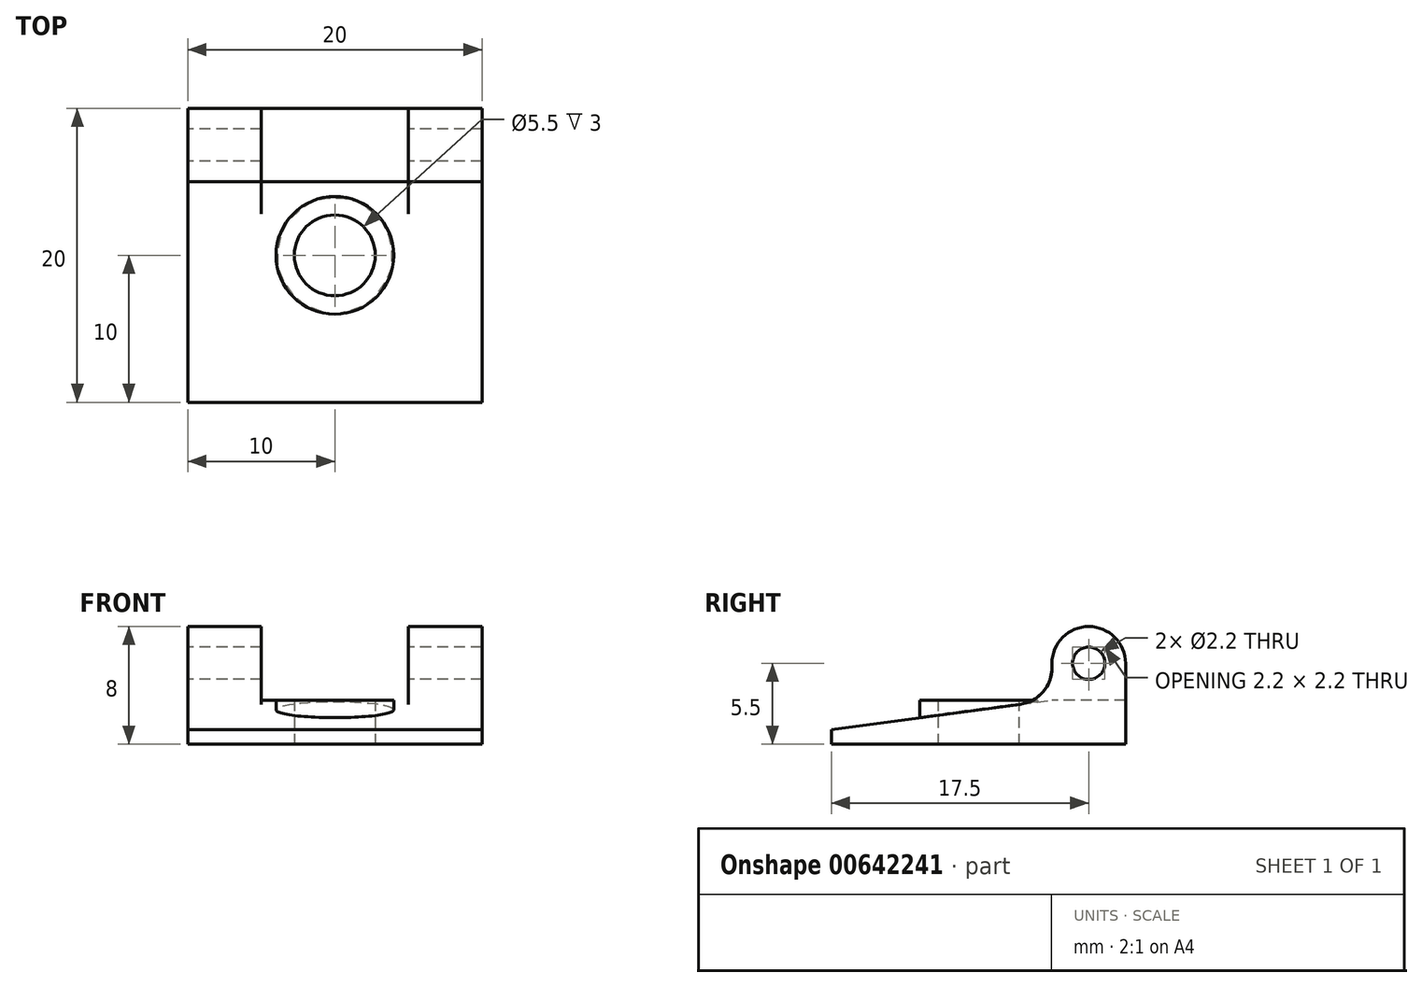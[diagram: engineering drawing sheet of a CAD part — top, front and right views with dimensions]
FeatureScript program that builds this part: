
annotation { "Feature Type Name" : "Feature", "Feature Type Description" : "" }
export const myFeature = defineFeature(function(context is Context, id is Id, definition is map)
    precondition{}
    {
        {
            var Q0;
            Q0=qCreatedBy(makeId("Top.planeOp"),FACE);
            var sketch = newSketch(context, id + "F0", { "sketchPlane" : qUnion([Q0])});
            skLineSegment(sketch, "E0.bottom", {"start": v(0, 0) * mm, "end": v(20, 0) * mm});
            skLineSegment(sketch, "E0.top", {"start": v(0, 20) * mm, "end": v(20, 20) * mm});
            skLineSegment(sketch, "E0.left", {"start": v(0, 0) * mm, "end": v(0, 20) * mm});
            skLineSegment(sketch, "E0.right", {"start": v(20, 0) * mm, "end": v(20, 20) * mm});
            skCircle(sketch, "E1", {"center": v(10, 10) * mm, "radius": 2.75 * mm});
            skCircle(sketch, "E2", {"center": v(10, 10) * mm, "radius": 4 * mm});
            skSolve(sketch);
        }
        {
            var Q0;
            Q0=makeQuery(id+"F0.imprint","IMPRINT",FACE,{"disambiguationData":[TD([[makeQuery(id+"F0.imprint","IMPRINT",EDGE,{"derivedFrom":sQuery(id+"F0.wireOp",EDGE,"E0.bottom")}),1.0]])]});
            extrude(context, id + "F1", {"entities" : qUnion([Q0]), "depth" : 4 * mm, "offsetDistance" : 25 * mm});
        }
        {
            var Q0;
            Q0=makeQuery(id+"F1.opExtrude","CAP_FACE",FACE,{"disambiguationData":[OSD([sQuery(id+"F0.wireOp",EDGE,"E0.bottom"),sQuery(id+"F0.wireOp",EDGE,"E0.top"),sQuery(id+"F0.wireOp",EDGE,"E0.left"),sQuery(id+"F0.wireOp",EDGE,"E0.right"),sQuery(id+"F0.wireOp",EDGE,"ZYH9QQmX-2PjE-aLZQ-Eazc-tA7TEWaIdW3q")])],"isStart":false});
            var Q1;
            Q1=makeQuery(id+"F0.imprint","IMPRINT",FACE,{"disambiguationData":[TD([[makeQuery(id+"F0.imprint","IMPRINT",EDGE,{"derivedFrom":sQuery(id+"F0.wireOp",EDGE,"E1")}),-1.0]])]});
            extrude(context, id + "F2", {"entities" : qUnion([Q0, Q1]), "operationType" : NewBodyOperationType.ADD, "depth" : 1 * mm, "offsetDistance" : 25 * mm});
        }
        {
            var Q0;
            Q0=makeQuery(id+"F2.opExtrude","CAP_FACE",FACE,{"disambiguationData":[OSD([sQuery(id+"F0.wireOp",EDGE,"E0.bottom"),sQuery(id+"F0.wireOp",EDGE,"E0.top"),sQuery(id+"F0.wireOp",EDGE,"E0.left"),sQuery(id+"F0.wireOp",EDGE,"E0.right"),sQuery(id+"F0.wireOp",EDGE,"ZYH9QQmX-2PjE-aLZQ-Eazc-tA7TEWaIdW3q")])],"isStart":false});
            var sketch = newSketch(context, id + "F3", { "sketchPlane" : qUnion([Q0])});
            skLineSegment(sketch, "E3.bottom", {"start": v(0, 15) * mm, "end": v(20, 15) * mm});
            skLineSegment(sketch, "E3.top", {"start": v(0, 20) * mm, "end": v(20, 20) * mm});
            skLineSegment(sketch, "E3.left", {"start": v(0, 15) * mm, "end": v(0, 20) * mm});
            skLineSegment(sketch, "E3.right", {"start": v(20, 15) * mm, "end": v(20, 20) * mm});
            skLineSegment(sketch, "E4.bottom", {"start": v(5, 20) * mm, "end": v(15, 20) * mm});
            skLineSegment(sketch, "E4.top", {"start": v(5, 15) * mm, "end": v(15, 15) * mm});
            skLineSegment(sketch, "E4.left", {"start": v(5, 20) * mm, "end": v(5, 15) * mm});
            skLineSegment(sketch, "E4.right", {"start": v(15, 20) * mm, "end": v(15, 15) * mm});
            skSolve(sketch);
        }
        {
            var Q0;
            {var subQ0=sQuery(id+"F3.wireOp",EDGE,"E3.left");Q0=makeQuery(id+"F3.imprint","IMPRINT",FACE,{"disambiguationData":[TD([[makeQuery(id+"F3.imprint","IMPRINT",EDGE,{"derivedFrom":subQ0}),-1.0]])]});}
            var Q1;
            {var subQ0=sQuery(id+"F3.wireOp",EDGE,"E3.right");Q1=makeQuery(id+"F3.imprint","IMPRINT",FACE,{"disambiguationData":[TD([[makeQuery(id+"F3.imprint","IMPRINT",EDGE,{"derivedFrom":subQ0}),1.0]])]});}
            extrude(context, id + "F4", {"entities" : qUnion([Q0, Q1]), "operationType" : NewBodyOperationType.ADD, "depth" : 5 * mm, "offsetDistance" : 25 * mm});
        }
        {
            var Q0;
            Q0=makeQuery(id+"F2.opExtrude","CAP_EDGE",EDGE,{"disambiguationData":[OSD([sQuery(id+"F0.wireOp",EDGE,"E0.bottom")])],"isStart":false});
            chamfer(context, id + "F5", {"entities" : qUnion([Q0]), "chamferType" : ChamferType.TWO_OFFSETS, "width1" : 15 * mm, "oppositeDirection" : false, "width2" : 2 * mm, "tangentPropagation" : true});
        }
        {
            var Q0;
            {var subQ0=sQuery(id+"F3.wireOp",EDGE,"E3.bottom");Q0=makeQuery(id+"F5.opChamfer","BLEND_EDGE",EDGE,{"blendedFrom":[makeQuery(id+"F2.opExtrude","CAP_EDGE",EDGE,{"disambiguationData":[OSD([sQuery(id+"F0.wireOp",EDGE,"E0.bottom")])],"isStart":false}),makeQuery(id+"F4.opExtrude","SWEPT_FACE",FACE,{"disambiguationData":[OSD([subQ0]),TDD([makeQuery(id+"F3.imprint","IMPRINT",EDGE,{"disambiguationData":[TD([[makeQuery(id+"F3.imprint","INTERSECT",VERTEX,{"derivedFrom":[makeQuery(id+"F2.opExtrude","CAP_EDGE",EDGE,{"disambiguationData":[OSD([sQuery(id+"F0.wireOp",EDGE,"E0.left")])],"isStart":false}),subQ0,sQuery(id+"F3.wireOp",EDGE,"E3.left")]}),-1.0]])],"derivedFrom":subQ0})])]})],"blendedInto":[makeQuery(id+"F4.opExtrude","SWEPT_FACE",FACE,{"disambiguationData":[OSD([subQ0]),TDD([makeQuery(id+"F3.imprint","IMPRINT",EDGE,{"disambiguationData":[TD([[makeQuery(id+"F3.imprint","INTERSECT",VERTEX,{"derivedFrom":[makeQuery(id+"F2.opExtrude","CAP_EDGE",EDGE,{"disambiguationData":[OSD([sQuery(id+"F0.wireOp",EDGE,"E0.left")])],"isStart":false}),subQ0,sQuery(id+"F3.wireOp",EDGE,"E3.left")]}),-1.0]])],"derivedFrom":subQ0})])]})]});}
            var Q1;
            {var subQ0=sQuery(id+"F3.wireOp",EDGE,"E3.bottom");Q1=makeQuery(id+"F4.opExtrude","CAP_EDGE",EDGE,{"disambiguationData":[OSD([subQ0]),TDD([makeQuery(id+"F3.imprint","IMPRINT",EDGE,{"disambiguationData":[TD([[makeQuery(id+"F3.imprint","INTERSECT",VERTEX,{"derivedFrom":[makeQuery(id+"F2.opExtrude","CAP_EDGE",EDGE,{"disambiguationData":[OSD([sQuery(id+"F0.wireOp",EDGE,"E0.left")])],"isStart":false}),subQ0,sQuery(id+"F3.wireOp",EDGE,"E3.left")]}),-1.0]])],"derivedFrom":subQ0})])],"isStart":false});}
            var Q2;
            {var subQ0=sQuery(id+"F3.wireOp",EDGE,"E3.bottom");Q2=makeQuery(id+"F5.opChamfer","BLEND_EDGE",EDGE,{"blendedFrom":[makeQuery(id+"F2.opExtrude","CAP_EDGE",EDGE,{"disambiguationData":[OSD([sQuery(id+"F0.wireOp",EDGE,"E0.bottom")])],"isStart":false}),makeQuery(id+"F4.opExtrude","SWEPT_FACE",FACE,{"disambiguationData":[OSD([subQ0]),TDD([makeQuery(id+"F3.imprint","IMPRINT",EDGE,{"disambiguationData":[TD([[makeQuery(id+"F3.imprint","INTERSECT",VERTEX,{"derivedFrom":[makeQuery(id+"F2.opExtrude","CAP_EDGE",EDGE,{"disambiguationData":[OSD([sQuery(id+"F0.wireOp",EDGE,"E0.right")])],"isStart":false}),subQ0,sQuery(id+"F3.wireOp",EDGE,"E3.right")]}),1.0]])],"derivedFrom":subQ0})])]})],"blendedInto":[makeQuery(id+"F4.opExtrude","SWEPT_FACE",FACE,{"disambiguationData":[OSD([subQ0]),TDD([makeQuery(id+"F3.imprint","IMPRINT",EDGE,{"disambiguationData":[TD([[makeQuery(id+"F3.imprint","INTERSECT",VERTEX,{"derivedFrom":[makeQuery(id+"F2.opExtrude","CAP_EDGE",EDGE,{"disambiguationData":[OSD([sQuery(id+"F0.wireOp",EDGE,"E0.right")])],"isStart":false}),subQ0,sQuery(id+"F3.wireOp",EDGE,"E3.right")]}),1.0]])],"derivedFrom":subQ0})])]})]});}
            var Q3;
            {var subQ0=sQuery(id+"F3.wireOp",EDGE,"E3.bottom");Q3=makeQuery(id+"F4.opExtrude","CAP_EDGE",EDGE,{"disambiguationData":[OSD([subQ0]),TDD([makeQuery(id+"F3.imprint","IMPRINT",EDGE,{"disambiguationData":[TD([[makeQuery(id+"F3.imprint","INTERSECT",VERTEX,{"derivedFrom":[makeQuery(id+"F2.opExtrude","CAP_EDGE",EDGE,{"disambiguationData":[OSD([sQuery(id+"F0.wireOp",EDGE,"E0.right")])],"isStart":false}),subQ0,sQuery(id+"F3.wireOp",EDGE,"E3.right")]}),1.0]])],"derivedFrom":subQ0})])],"isStart":false});}
            var Q4;
            {var subQ0=sQuery(id+"F3.wireOp",EDGE,"E3.top");Q4=makeQuery(id+"F4.opExtrude","CAP_EDGE",EDGE,{"disambiguationData":[OSD([subQ0]),TDD([makeQuery(id+"F3.imprint","IMPRINT",EDGE,{"disambiguationData":[TD([[makeQuery(id+"F3.imprint","INTERSECT",VERTEX,{"derivedFrom":[makeQuery(id+"F2.opExtrude","CAP_EDGE",EDGE,{"disambiguationData":[OSD([sQuery(id+"F0.wireOp",EDGE,"E0.left")])],"isStart":false}),subQ0,sQuery(id+"F3.wireOp",EDGE,"E3.left")]}),-1.0]])],"derivedFrom":subQ0})])],"isStart":false});}
            var Q5;
            {var subQ0=sQuery(id+"F3.wireOp",EDGE,"E3.top");Q5=makeQuery(id+"F4.opExtrude","CAP_EDGE",EDGE,{"disambiguationData":[OSD([subQ0]),TDD([makeQuery(id+"F3.imprint","IMPRINT",EDGE,{"disambiguationData":[TD([[makeQuery(id+"F3.imprint","INTERSECT",VERTEX,{"derivedFrom":[makeQuery(id+"F2.opExtrude","CAP_EDGE",EDGE,{"disambiguationData":[OSD([sQuery(id+"F0.wireOp",EDGE,"E0.right")])],"isStart":false}),subQ0,sQuery(id+"F3.wireOp",EDGE,"E3.right")]}),1.0]])],"derivedFrom":subQ0})])],"isStart":false});}
            fillet(context, id + "F6", {"entities" : qUnion([Q0, Q1, Q2, Q3, Q4, Q5]), "radius" : 2.5 * mm, "tangentPropagation" : true, "allowEdgeOverflow" : false});
        }
        {
            var Q0;
            {var subQ0=sQuery(id+"F0.wireOp",EDGE,"E0.left");Q0=makeQuery(id+"F4.boolean.opBoolean","MERGE",FACE,{"derivedFrom":[makeQuery(id+"F2.boolean.opBoolean","MERGE",FACE,{"derivedFrom":[makeQuery(id+"F1.opExtrude","SWEPT_FACE",FACE,{"disambiguationData":[OSD([subQ0])]}),makeQuery(id+"F2.opExtrude","SWEPT_FACE",FACE,{"disambiguationData":[OSD([subQ0])]})]}),makeQuery(id+"F4.opExtrude","SWEPT_FACE",FACE,{"disambiguationData":[OSD([sQuery(id+"F3.wireOp",EDGE,"E3.left")])]})]});}
            var sketch = newSketch(context, id + "F7", { "sketchPlane" : qUnion([Q0])});
            skCircle(sketch, "E5", {"center": v(-17.5, 7.5) * mm, "radius": 1.1 * mm});
            skSolve(sketch);
        }
        {
            var Q0;
            Q0=makeQuery(id+"F7.imprint","IMPRINT",FACE,{"disambiguationData":[TD([[makeQuery(id+"F7.imprint","IMPRINT",EDGE,{"derivedFrom":sQuery(id+"F7.wireOp",EDGE,"E5")}),1.0]])]});
            extrude(context, id + "F8", {"entities" : qUnion([Q0]), "operationType" : NewBodyOperationType.REMOVE, "oppositeDirection" : true, "depth" : 25 * mm, "offsetDistance" : 25 * mm});
        }
        {
            var Q0;
            Q0=makeQuery(id+"F0.imprint","IMPRINT",FACE,{"disambiguationData":[TD([[makeQuery(id+"F0.imprint","IMPRINT",EDGE,{"derivedFrom":sQuery(id+"F0.wireOp",EDGE,"E1")}),-1.0]])]});
            extrude(context, id + "F9", {"entities" : qUnion([Q0]), "depth" : 5 * mm, "offsetDistance" : 25 * mm});
        }
        {
            var Q0;
            Q0=makeQuery(id+"F0.imprint","IMPRINT",FACE,{"disambiguationData":[TD([[makeQuery(id+"F0.imprint","IMPRINT",EDGE,{"derivedFrom":sQuery(id+"F0.wireOp",EDGE,"E1")}),1.0]])]});
            extrude(context, id + "F10", {"entities" : qUnion([Q0]), "operationType" : NewBodyOperationType.ADD, "depth" : 2 * mm, "offsetDistance" : 25 * mm});
        }
        {
            var Q0;
            Q0=makeQuery(id+"F0.imprint","IMPRINT",FACE,{"disambiguationData":[TD([[makeQuery(id+"F0.imprint","IMPRINT",EDGE,{"derivedFrom":sQuery(id+"F0.wireOp",EDGE,"E0.bottom")}),1.0]])]});
            var Q1;
            Q1=makeQuery(id+"F0.imprint","IMPRINT",FACE,{"disambiguationData":[TD([[makeQuery(id+"F0.imprint","IMPRINT",EDGE,{"derivedFrom":sQuery(id+"F0.wireOp",EDGE,"E1")}),-1.0]])]});
            var Q2;
            Q2=makeQuery(id+"F0.imprint","IMPRINT",FACE,{"disambiguationData":[TD([[makeQuery(id+"F0.imprint","IMPRINT",EDGE,{"derivedFrom":sQuery(id+"F0.wireOp",EDGE,"E1")}),1.0]])]});
            extrude(context, id + "F11", {"entities" : qUnion([Q0, Q1, Q2]), "operationType" : NewBodyOperationType.REMOVE, "depth" : 2 * mm, "offsetDistance" : 25 * mm});
        }
    });
